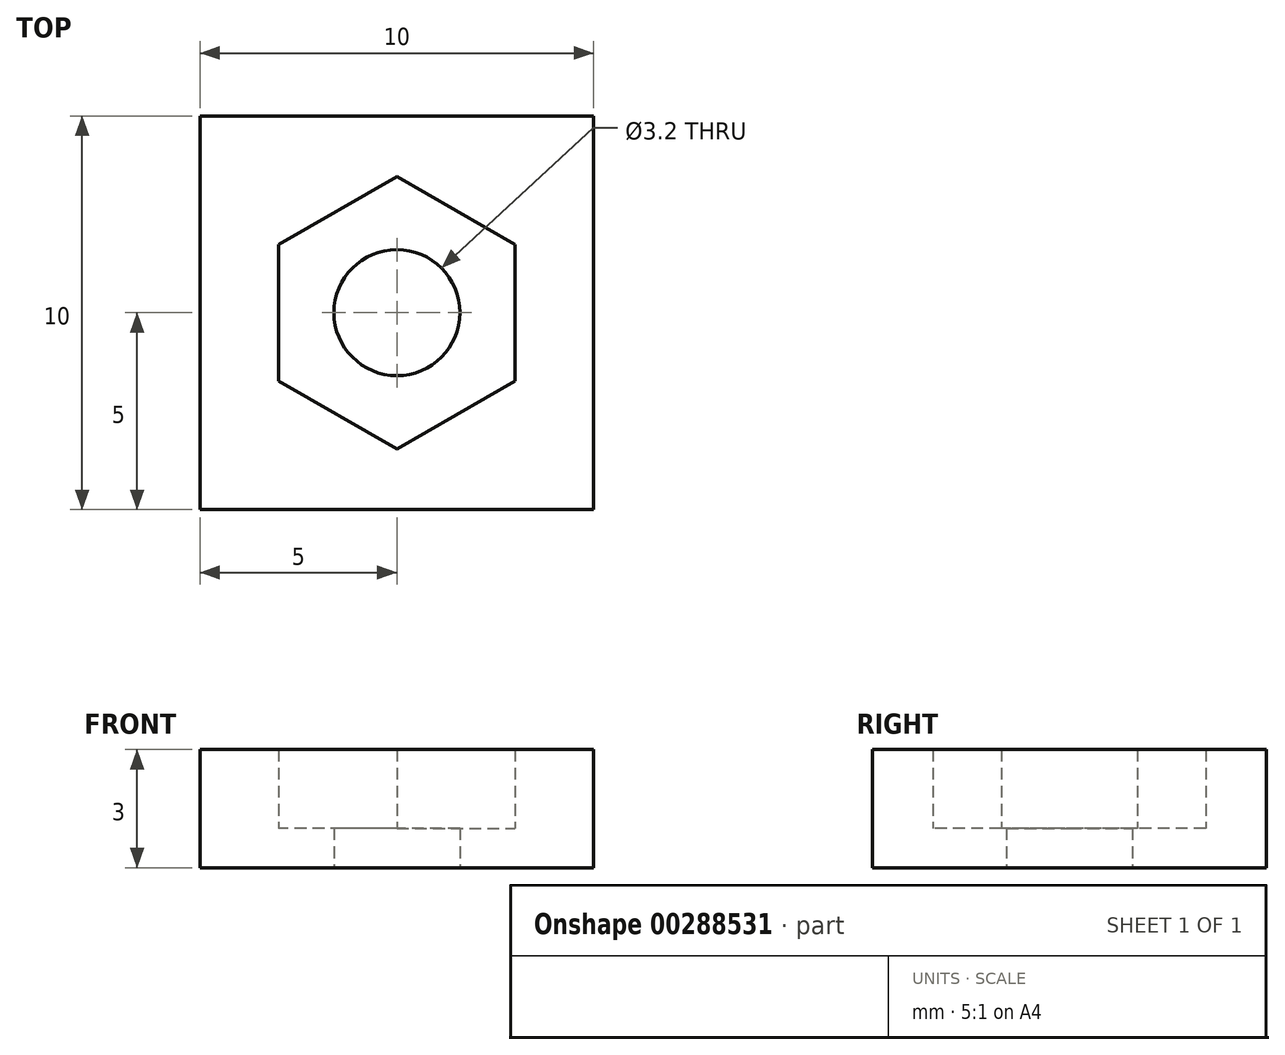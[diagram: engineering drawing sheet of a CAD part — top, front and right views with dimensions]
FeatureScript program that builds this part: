
annotation { "Feature Type Name" : "Feature", "Feature Type Description" : "" }
export const myFeature = defineFeature(function(context is Context, id is Id, definition is map)
    precondition{}
    {
        {
            var Q0;
            Q0=qCreatedBy(makeId("Top.planeOp"),FACE);
            var sketch = newSketch(context, id + "F0", { "sketchPlane" : qUnion([Q0])});
            skLineSegment(sketch, "E0.bottom", {"start": v(5, -5) * mm, "end": v(-5, -5) * mm});
            skLineSegment(sketch, "E0.top", {"start": v(5, 5) * mm, "end": v(-5, 5) * mm});
            skLineSegment(sketch, "E0.left", {"start": v(5, -5) * mm, "end": v(5, 5) * mm});
            skLineSegment(sketch, "E0.right", {"start": v(-5, -5) * mm, "end": v(-5, 5) * mm});
            skPoint(sketch, "E0.middle", {"position": v(0, 0) * mm});
            skCircle(sketch, "E1", {"center": v(0, 0) * mm, "radius": 1.6 * mm});
            skCircle(sketch, "E2.cCircle", {"center": v(0, 0) * mm, "radius": 3 * mm, "construction": true});
            skLineSegment(sketch, "E2.0", {"start": v(3, 1.73) * mm, "end": v(3, -1.73) * mm});
            skLineSegment(sketch, "E2.1", {"start": v(3, -1.73) * mm, "end": v(0, -3.46) * mm});
            skLineSegment(sketch, "E2.2", {"start": v(0, -3.46) * mm, "end": v(-3, -1.73) * mm});
            skLineSegment(sketch, "E2.3", {"start": v(-3, -1.73) * mm, "end": v(-3, 1.73) * mm});
            skLineSegment(sketch, "E2.4", {"start": v(-3, 1.73) * mm, "end": v(0, 3.46) * mm});
            skLineSegment(sketch, "E2.5", {"start": v(0, 3.46) * mm, "end": v(3, 1.73) * mm});
            skPoint(sketch, "E2.0.midPoint", {"position": v(3, 0) * mm});
            skPoint(sketch, "E3.visualSharp", {"position": v(-3, 1.73) * mm});
            skLineSegment(sketch, "E3.filletArc", {"start": v(-3, 1.73) * mm, "end": v(-3, 1.73) * mm});
            skPoint(sketch, "E4.visualSharp", {"position": v(0, 3.46) * mm});
            skLineSegment(sketch, "E4.filletArc", {"start": v(0, 3.46) * mm, "end": v(0, 3.46) * mm});
            skPoint(sketch, "E5.visualSharp", {"position": v(3, 1.73) * mm});
            skLineSegment(sketch, "E5.filletArc", {"start": v(3, 1.73) * mm, "end": v(3, 1.73) * mm});
            skPoint(sketch, "E6.visualSharp", {"position": v(3, -1.73) * mm});
            skLineSegment(sketch, "E6.filletArc", {"start": v(3, -1.73) * mm, "end": v(3, -1.73) * mm});
            skPoint(sketch, "E7.visualSharp", {"position": v(0, -3.46) * mm});
            skLineSegment(sketch, "E7.filletArc", {"start": v(0, -3.46) * mm, "end": v(0, -3.46) * mm});
            skPoint(sketch, "E8.visualSharp", {"position": v(-3, -1.73) * mm});
            skLineSegment(sketch, "E8.filletArc", {"start": v(-3, -1.73) * mm, "end": v(-3, -1.73) * mm});
            skSolve(sketch);
        }
        {
            var Q0;
            Q0=makeQuery(id+"F0.imprint","IMPRINT",FACE,{"disambiguationData":[TD([[makeQuery(id+"F0.imprint","IMPRINT",EDGE,{"derivedFrom":sQuery(id+"F0.wireOp",EDGE,"E0.bottom")}),-1.0]])]});
            extrude(context, id + "F1", {"entities" : qUnion([Q0]), "depth" : 3 * mm});
        }
        {
            var Q0;
            Q0=makeQuery(id+"F0.imprint","IMPRINT",FACE,{"disambiguationData":[TD([[makeQuery(id+"F0.imprint","IMPRINT",EDGE,{"derivedFrom":sQuery(id+"F0.wireOp",EDGE,"E1")}),-1.0]])]});
            extrude(context, id + "F2", {"entities" : qUnion([Q0]), "operationType" : NewBodyOperationType.ADD, "depth" : 1 * mm});
        }
    });
